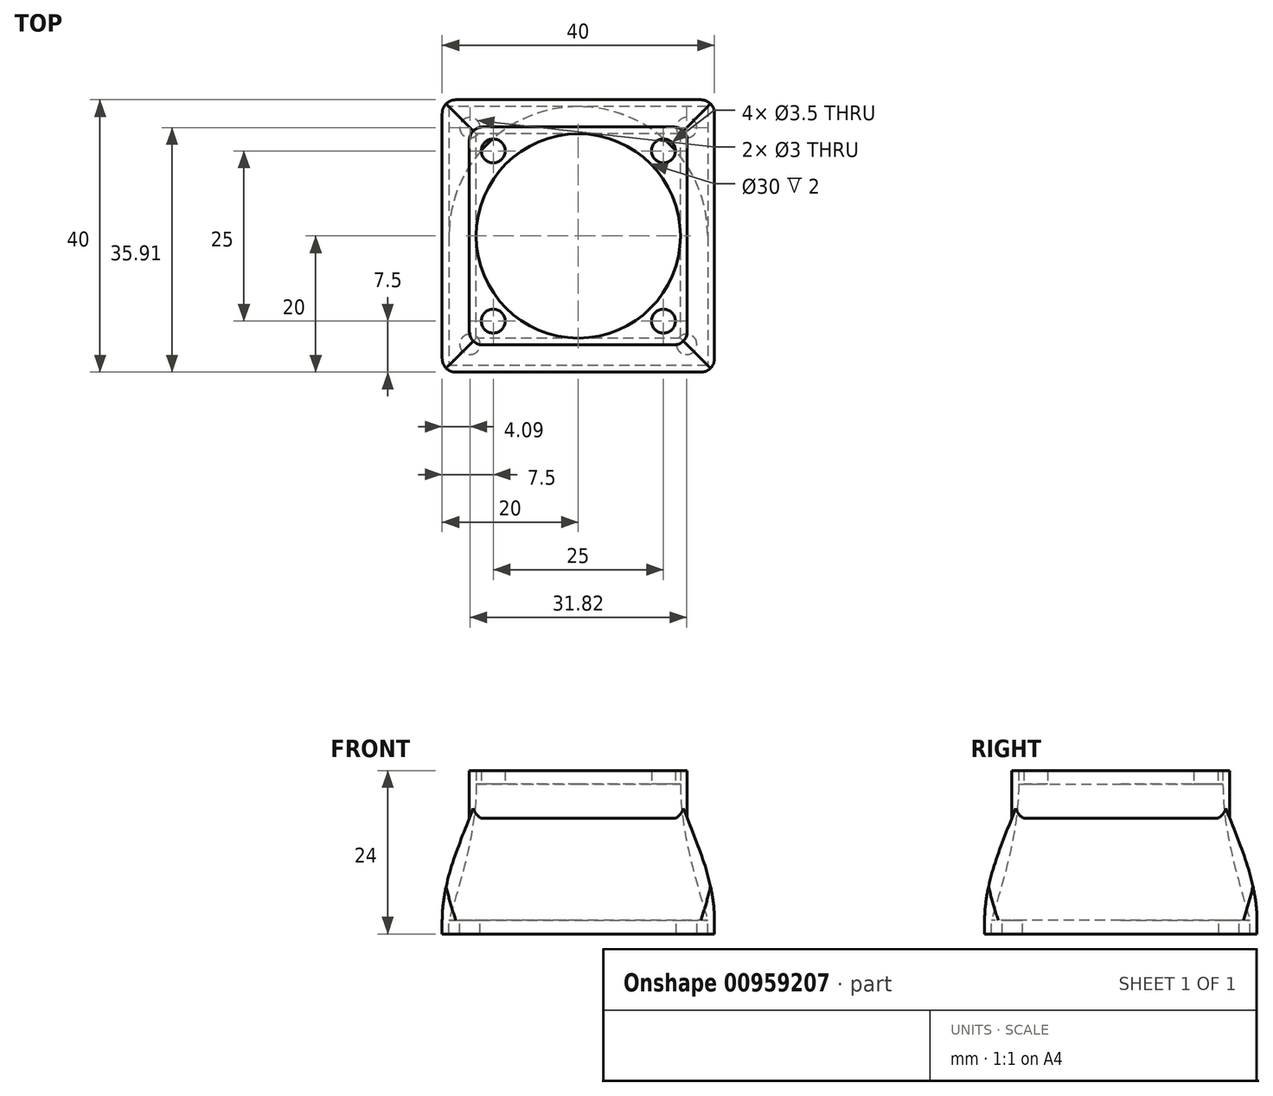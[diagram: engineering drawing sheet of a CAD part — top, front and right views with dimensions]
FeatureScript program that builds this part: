
annotation { "Feature Type Name" : "Feature", "Feature Type Description" : "" }
export const myFeature = defineFeature(function(context is Context, id is Id, definition is map)
    precondition{}
    {
        {
            var Q0;
            Q0=qCreatedBy(makeId("Top.planeOp"),FACE);
            var sketch = newSketch(context, id + "F0", { "sketchPlane" : qUnion([Q0])});
            skLineSegment(sketch, "E0.bottom", {"start": v(20, 20) * mm, "end": v(-20, 20) * mm});
            skLineSegment(sketch, "E0.top", {"start": v(20, -20) * mm, "end": v(-20, -20) * mm});
            skLineSegment(sketch, "E0.left", {"start": v(20, 20) * mm, "end": v(20, -20) * mm});
            skLineSegment(sketch, "E0.right", {"start": v(-20, 20) * mm, "end": v(-20, -20) * mm});
            skPoint(sketch, "E0.middle", {"position": v(0, 0) * mm});
            skSolve(sketch);
        }
        {
            var Q0;
            Q0=makeQuery(id+"F0.imprint","IMPRINT",FACE,{"disambiguationData":[TD([[makeQuery(id+"F0.imprint","IMPRINT",EDGE,{"derivedFrom":sQuery(id+"F0.wireOp",EDGE,"E0.bottom")}),1.0]])]});
            cPlane(context, id + "F1", {"entities" : qUnion([Q0]), "cplaneType" : CPlaneType.OFFSET, "offset" : 15 * mm, "width" : 150 * mm, "height" : 150 * mm});
        }
        {
            var Q0;
            Q0=qCreatedBy(id+"F1.planeOp",FACE);
            var sketch = newSketch(context, id + "F2", { "sketchPlane" : qUnion([Q0])});
            skLineSegment(sketch, "E1.bottom", {"start": v(16, -16) * mm, "end": v(-16, -16) * mm});
            skLineSegment(sketch, "E1.top", {"start": v(16, 16) * mm, "end": v(-16, 16) * mm});
            skLineSegment(sketch, "E1.left", {"start": v(16, -16) * mm, "end": v(16, 16) * mm});
            skLineSegment(sketch, "E1.right", {"start": v(-16, -16) * mm, "end": v(-16, 16) * mm});
            skPoint(sketch, "E1.middle", {"position": v(0, 0) * mm});
            skSolve(sketch);
        }
        {
            var Q0;
            Q0=makeQuery(id+"F0.imprint","IMPRINT",FACE,{"disambiguationData":[TD([[makeQuery(id+"F0.imprint","IMPRINT",EDGE,{"derivedFrom":sQuery(id+"F0.wireOp",EDGE,"E0.bottom")}),1.0]])]});
            var Q1;
            Q1=makeQuery(id+"F2.imprint","IMPRINT",FACE,{"disambiguationData":[TD([[makeQuery(id+"F2.imprint","IMPRINT",EDGE,{"derivedFrom":sQuery(id+"F2.wireOp",EDGE,"E1.bottom")}),-1.0]])]});
            loft(context, id + "F3", {"startCondition" : LoftEndDerivativeType.NORMAL_TO_PROFILE, "startMagnitude" : 1, "sheetProfilesArray" : [{ "sheetProfileEntities" : qUnion([Q0]) }, { "sheetProfileEntities" : qUnion([Q1]) }]});
        }
        {
            var Q0;
            Q0=makeQuery(id+"F2.imprint","IMPRINT",FACE,{"disambiguationData":[TD([[makeQuery(id+"F2.imprint","IMPRINT",EDGE,{"derivedFrom":sQuery(id+"F2.wireOp",EDGE,"E1.bottom")}),-1.0]])]});
            extrude(context, id + "F4", {"entities" : qUnion([Q0]), "operationType" : NewBodyOperationType.ADD, "depth" : 5 * mm, "offsetDistance" : 25 * mm});
        }
        {
            var Q0;
            Q0=makeQuery(id+"F4.opExtrude","CAP_FACE",FACE,{"disambiguationData":[OSD([sQuery(id+"F2.wireOp",EDGE,"E1.bottom"),sQuery(id+"F2.wireOp",EDGE,"E1.top"),sQuery(id+"F2.wireOp",EDGE,"E1.left"),sQuery(id+"F2.wireOp",EDGE,"E1.right")])],"isStart":false});
            var sketch = newSketch(context, id + "F5", { "sketchPlane" : qUnion([Q0])});
            skCircle(sketch, "E2", {"center": v(0, 0) * mm, "radius": 13.5 * mm, "construction": true});
            skCircle(sketch, "E3", {"center": v(0, 0) * mm, "radius": 17.68 * mm, "construction": true});
            skLineSegment(sketch, "E4", {"start": v(16, -16) * mm, "end": v(-16, 16) * mm, "construction": true});
            skLineSegment(sketch, "E5", {"start": v(16, 16) * mm, "end": v(-16, -16) * mm, "construction": true});
            skCircle(sketch, "E6", {"center": v(12.5, -12.5) * mm, "radius": 1.25 * mm, "construction": true});
            skCircle(sketch, "E7", {"center": v(-12.5, -12.5) * mm, "radius": 1.25 * mm, "construction": true});
            skCircle(sketch, "E8", {"center": v(12.5, 12.5) * mm, "radius": 1.25 * mm, "construction": true});
            skCircle(sketch, "E9", {"center": v(-12.5, 12.5) * mm, "radius": 1.25 * mm, "construction": true});
            skLineSegment(sketch, "E10.bottom", {"start": v(15, -15) * mm, "end": v(-15, -15) * mm});
            skLineSegment(sketch, "E10.top", {"start": v(15, 15) * mm, "end": v(-15, 15) * mm});
            skLineSegment(sketch, "E10.left", {"start": v(15, -15) * mm, "end": v(15, 15) * mm});
            skLineSegment(sketch, "E10.right", {"start": v(-15, -15) * mm, "end": v(-15, 15) * mm});
            skSolve(sketch);
        }
        {
            var Q0;
            Q0=makeQuery(id+"F3.opLoft","CAP_FACE",FACE,{"disambiguationData":[OSD([makeQuery(id+"F0.imprint","IMPRINT",FACE,{"disambiguationData":[TD([[makeQuery(id+"F0.imprint","IMPRINT",EDGE,{"derivedFrom":sQuery(id+"F0.wireOp",EDGE,"E0.bottom")}),1.0]])]})])],"isStart":true});
            var sketch = newSketch(context, id + "F6", { "sketchPlane" : qUnion([Q0])});
            skPoint(sketch, "E11.middle", {"position": v(0, 0) * mm});
            skCircle(sketch, "E12", {"center": v(0, 0) * mm, "radius": 21.21 * mm, "construction": true});
            skLineSegment(sketch, "E13", {"start": v(-20, 20) * mm, "end": v(20, -20) * mm, "construction": true});
            skLineSegment(sketch, "E14", {"start": v(20, 20) * mm, "end": v(-20, -20) * mm, "construction": true});
            skCircle(sketch, "E15", {"center": v(-15, 15) * mm, "radius": 1.25 * mm, "construction": true});
            skCircle(sketch, "E16", {"center": v(15, 15) * mm, "radius": 1.25 * mm, "construction": true});
            skCircle(sketch, "E17", {"center": v(15, -15) * mm, "radius": 1.25 * mm, "construction": true});
            skCircle(sketch, "E18", {"center": v(-15, -15) * mm, "radius": 1.25 * mm, "construction": true});
            skLineSegment(sketch, "E19.bottom", {"start": v(19, -19) * mm, "end": v(-19, -19) * mm});
            skLineSegment(sketch, "E19.top", {"start": v(19, 19) * mm, "end": v(-19, 19) * mm});
            skLineSegment(sketch, "E19.left", {"start": v(19, -19) * mm, "end": v(19, 19) * mm});
            skLineSegment(sketch, "E19.right", {"start": v(-19, -19) * mm, "end": v(-19, 19) * mm});
            skSolve(sketch);
        }
        {
            var Q1;
            Q1=makeQuery(id+"F5.imprint","IMPRINT",FACE,{"disambiguationData":[TD([[makeQuery(id+"F5.imprint","IMPRINT",EDGE,{"derivedFrom":sQuery(id+"F5.wireOp",EDGE,"E10.bottom")}),-1.0]])]});
            var Q2;
            Q2=makeQuery(id+"F6.imprint","IMPRINT",FACE,{"disambiguationData":[TD([[makeQuery(id+"F6.imprint","IMPRINT",EDGE,{"derivedFrom":sQuery(id+"F6.wireOp",EDGE,"E19.bottom")}),-1.0]])]});
            loft(context, id + "F7", {"operationType" : NewBodyOperationType.REMOVE, "startCondition" : LoftEndDerivativeType.NORMAL_TO_PROFILE, "startMagnitude" : 1, "sheetProfilesArray" : [{ "sheetProfileEntities" : qUnion([Q1]) }, { "sheetProfileEntities" : qUnion([Q2]) }]});
        }
        {
            var Q0;
            Q0=makeQuery(id+"F3.opLoft","CAP_FACE",FACE,{"disambiguationData":[OSD([makeQuery(id+"F0.imprint","IMPRINT",FACE,{"disambiguationData":[TD([[makeQuery(id+"F0.imprint","IMPRINT",EDGE,{"derivedFrom":sQuery(id+"F0.wireOp",EDGE,"E0.bottom")}),1.0]])]})])],"isStart":true});
            var sketch = newSketch(context, id + "F8", { "sketchPlane" : qUnion([Q0])});
            skLineSegment(sketch, "E20.bottom", {"start": v(-20, 20) * mm, "end": v(20, 20) * mm});
            skLineSegment(sketch, "E20.top", {"start": v(-20, -20) * mm, "end": v(20, -20) * mm});
            skLineSegment(sketch, "E20.left", {"start": v(-20, 20) * mm, "end": v(-20, -20) * mm});
            skLineSegment(sketch, "E20.right", {"start": v(20, 20) * mm, "end": v(20, -20) * mm});
            skCircle(sketch, "E21", {"center": v(0, 0) * mm, "radius": 19 * mm});
            skLineSegment(sketch, "E22", {"start": v(-20, -20) * mm, "end": v(20, 20) * mm, "construction": true});
            skLineSegment(sketch, "E23", {"start": v(-20, 20) * mm, "end": v(20, -20) * mm, "construction": true});
            skCircle(sketch, "E24", {"center": v(0, 0) * mm, "radius": 22.5 * mm, "construction": true});
            skCircle(sketch, "E25", {"center": v(-15.9, -15.9) * mm, "radius": 1.5 * mm});
            skCircle(sketch, "E26.MirrorC", {"center": v(15.9, 15.9) * mm, "radius": 1.5 * mm});
            skCircle(sketch, "E27.MirrorC", {"center": v(15.9, -15.9) * mm, "radius": 1.5 * mm});
            skCircle(sketch, "E28.MirrorC", {"center": v(-15.9, 15.9) * mm, "radius": 1.5 * mm});
            skSolve(sketch);
        }
        {
            var Q0;
            Q0=makeQuery(id+"F8.imprint","IMPRINT",FACE,{"disambiguationData":[TD([[makeQuery(id+"F8.imprint","IMPRINT",EDGE,{"derivedFrom":sQuery(id+"F8.wireOp",EDGE,"E20.bottom")}),-1.0]])]});
            var Q1;
            Q1=makeQuery(id+"F8.imprint","IMPRINT",FACE,{"disambiguationData":[TD([[makeQuery(id+"F8.imprint","IMPRINT",EDGE,{"derivedFrom":sQuery(id+"F8.wireOp",EDGE,"E28.MirrorC")}),1.0]])]});
            var Q2;
            Q2=makeQuery(id+"F8.imprint","IMPRINT",FACE,{"disambiguationData":[TD([[makeQuery(id+"F8.imprint","IMPRINT",EDGE,{"derivedFrom":sQuery(id+"F8.wireOp",EDGE,"E26.MirrorC")}),1.0]])]});
            var Q3;
            Q3=makeQuery(id+"F8.imprint","IMPRINT",FACE,{"disambiguationData":[TD([[makeQuery(id+"F8.imprint","IMPRINT",EDGE,{"derivedFrom":sQuery(id+"F8.wireOp",EDGE,"E27.MirrorC")}),-1.0]])]});
            var Q4;
            Q4=makeQuery(id+"F8.imprint","IMPRINT",FACE,{"disambiguationData":[TD([[makeQuery(id+"F8.imprint","IMPRINT",EDGE,{"derivedFrom":sQuery(id+"F8.wireOp",EDGE,"E25")}),-1.0]])]});
            extrude(context, id + "F9", {"entities" : qUnion([Q0, Q1, Q2, Q3, Q4]), "operationType" : NewBodyOperationType.ADD, "depth" : 2 * mm, "offsetDistance" : 25 * mm});
        }
        {
            var Q0;
            Q0=makeQuery(id+"F4.opExtrude","CAP_FACE",FACE,{"disambiguationData":[OSD([sQuery(id+"F2.wireOp",EDGE,"E1.bottom"),sQuery(id+"F2.wireOp",EDGE,"E1.top"),sQuery(id+"F2.wireOp",EDGE,"E1.left"),sQuery(id+"F2.wireOp",EDGE,"E1.right")])],"isStart":false});
            var sketch = newSketch(context, id + "F10", { "sketchPlane" : qUnion([Q0])});
            skLineSegment(sketch, "E29.bottom", {"start": v(-16, -16) * mm, "end": v(16, -16) * mm});
            skLineSegment(sketch, "E29.top", {"start": v(-16, 16) * mm, "end": v(16, 16) * mm});
            skLineSegment(sketch, "E29.left", {"start": v(-16, -16) * mm, "end": v(-16, 16) * mm});
            skLineSegment(sketch, "E29.right", {"start": v(16, -16) * mm, "end": v(16, 16) * mm});
            skCircle(sketch, "E30", {"center": v(0, 0) * mm, "radius": 15 * mm});
            skCircle(sketch, "E31", {"center": v(0, 0) * mm, "radius": 17.68 * mm, "construction": true});
            skLineSegment(sketch, "E32", {"start": v(-16, -16) * mm, "end": v(16, 16) * mm, "construction": true});
            skLineSegment(sketch, "E33", {"start": v(16, -16) * mm, "end": v(-16, 16) * mm, "construction": true});
            skCircle(sketch, "E34", {"center": v(-12.5, -12.5) * mm, "radius": 1.75 * mm});
            skCircle(sketch, "E35", {"center": v(-12.5, 12.5) * mm, "radius": 1.75 * mm});
            skCircle(sketch, "E36", {"center": v(12.5, -12.5) * mm, "radius": 1.75 * mm});
            skCircle(sketch, "E37", {"center": v(12.5, 12.5) * mm, "radius": 1.75 * mm});
            skSolve(sketch);
        }
        {
            var Q0;
            Q0=makeQuery(id+"F10.imprint","IMPRINT",FACE,{"disambiguationData":[TD([[makeQuery(id+"F10.imprint","IMPRINT",EDGE,{"derivedFrom":sQuery(id+"F10.wireOp",EDGE,"E34")}),-1.0]])]});
            var Q1;
            Q1=makeQuery(id+"F10.imprint","IMPRINT",FACE,{"disambiguationData":[TD([[makeQuery(id+"F10.imprint","IMPRINT",EDGE,{"derivedFrom":sQuery(id+"F10.wireOp",EDGE,"E35")}),-1.0]])]});
            var Q2;
            Q2=makeQuery(id+"F10.imprint","IMPRINT",FACE,{"disambiguationData":[TD([[makeQuery(id+"F10.imprint","IMPRINT",EDGE,{"derivedFrom":sQuery(id+"F10.wireOp",EDGE,"E29.bottom")}),-1.0]])]});
            var Q3;
            Q3=makeQuery(id+"F10.imprint","IMPRINT",FACE,{"disambiguationData":[TD([[makeQuery(id+"F10.imprint","IMPRINT",EDGE,{"derivedFrom":sQuery(id+"F10.wireOp",EDGE,"E37")}),-1.0]])]});
            var Q4;
            Q4=makeQuery(id+"F10.imprint","IMPRINT",FACE,{"disambiguationData":[TD([[makeQuery(id+"F10.imprint","IMPRINT",EDGE,{"derivedFrom":sQuery(id+"F10.wireOp",EDGE,"E36")}),-1.0]])]});
            extrude(context, id + "F11", {"entities" : qUnion([Q0, Q1, Q2, Q3, Q4]), "operationType" : NewBodyOperationType.ADD, "depth" : 2 * mm, "offsetDistance" : 25 * mm});
        }
        {
            var Q0;
            Q0=makeQuery(id+"F11.boolean.opBoolean","MERGE",EDGE,{"derivedFrom":[makeQuery(id+"F4.opExtrude","SWEPT_EDGE",EDGE,{"disambiguationData":[OSD([sQuery(id+"F2.wireOp",EDGE,"E1.bottom"),sQuery(id+"F2.wireOp",EDGE,"E1.left")])]}),makeQuery(id+"F11.opExtrude","SWEPT_EDGE",EDGE,{"disambiguationData":[OSD([sQuery(id+"F10.wireOp",EDGE,"E29.bottom"),sQuery(id+"F10.wireOp",EDGE,"E29.right")])]})]});
            var Q1;
            Q1=makeQuery(id+"F11.boolean.opBoolean","MERGE",EDGE,{"derivedFrom":[makeQuery(id+"F4.opExtrude","SWEPT_EDGE",EDGE,{"disambiguationData":[OSD([sQuery(id+"F2.wireOp",EDGE,"E1.top"),sQuery(id+"F2.wireOp",EDGE,"E1.left")])]}),makeQuery(id+"F11.opExtrude","SWEPT_EDGE",EDGE,{"disambiguationData":[OSD([sQuery(id+"F10.wireOp",EDGE,"E29.top"),sQuery(id+"F10.wireOp",EDGE,"E29.right")])]})]});
            var Q2;
            Q2=makeQuery(id+"F11.boolean.opBoolean","MERGE",EDGE,{"derivedFrom":[makeQuery(id+"F4.opExtrude","SWEPT_EDGE",EDGE,{"disambiguationData":[OSD([sQuery(id+"F2.wireOp",EDGE,"E1.top"),sQuery(id+"F2.wireOp",EDGE,"E1.right")])]}),makeQuery(id+"F11.opExtrude","SWEPT_EDGE",EDGE,{"disambiguationData":[OSD([sQuery(id+"F10.wireOp",EDGE,"E29.top"),sQuery(id+"F10.wireOp",EDGE,"E29.left")])]})]});
            var Q3;
            Q3=makeQuery(id+"F11.boolean.opBoolean","MERGE",EDGE,{"derivedFrom":[makeQuery(id+"F4.opExtrude","SWEPT_EDGE",EDGE,{"disambiguationData":[OSD([sQuery(id+"F2.wireOp",EDGE,"E1.bottom"),sQuery(id+"F2.wireOp",EDGE,"E1.right")])]}),makeQuery(id+"F11.opExtrude","SWEPT_EDGE",EDGE,{"disambiguationData":[OSD([sQuery(id+"F10.wireOp",EDGE,"E29.bottom"),sQuery(id+"F10.wireOp",EDGE,"E29.left")])]})]});
            fillet(context, id + "F12", {"entities" : qUnion([Q0, Q1, Q2, Q3]), "radius" : 1.95 * mm, "tangentPropagation" : true, "allowEdgeOverflow" : false});
        }
        {
            var Q0;
            Q0=makeQuery(id+"F9.opExtrude","SWEPT_EDGE",EDGE,{"disambiguationData":[OSD([sQuery(id+"F8.wireOp",EDGE,"E20.bottom"),sQuery(id+"F8.wireOp",EDGE,"E20.left")])]});
            var Q1;
            Q1=makeQuery(id+"F9.opExtrude","SWEPT_EDGE",EDGE,{"disambiguationData":[OSD([sQuery(id+"F8.wireOp",EDGE,"E20.bottom"),sQuery(id+"F8.wireOp",EDGE,"E20.right")])]});
            var Q2;
            Q2=makeQuery(id+"F9.opExtrude","SWEPT_EDGE",EDGE,{"disambiguationData":[OSD([sQuery(id+"F8.wireOp",EDGE,"E20.top"),sQuery(id+"F8.wireOp",EDGE,"E20.right")])]});
            var Q3;
            Q3=makeQuery(id+"F9.opExtrude","SWEPT_EDGE",EDGE,{"disambiguationData":[OSD([sQuery(id+"F8.wireOp",EDGE,"E20.top"),sQuery(id+"F8.wireOp",EDGE,"E20.left")])]});
            fillet(context, id + "F13", {"entities" : qUnion([Q0, Q1, Q2, Q3]), "radius" : 2 * mm, "allowEdgeOverflow" : false});
        }
    });
